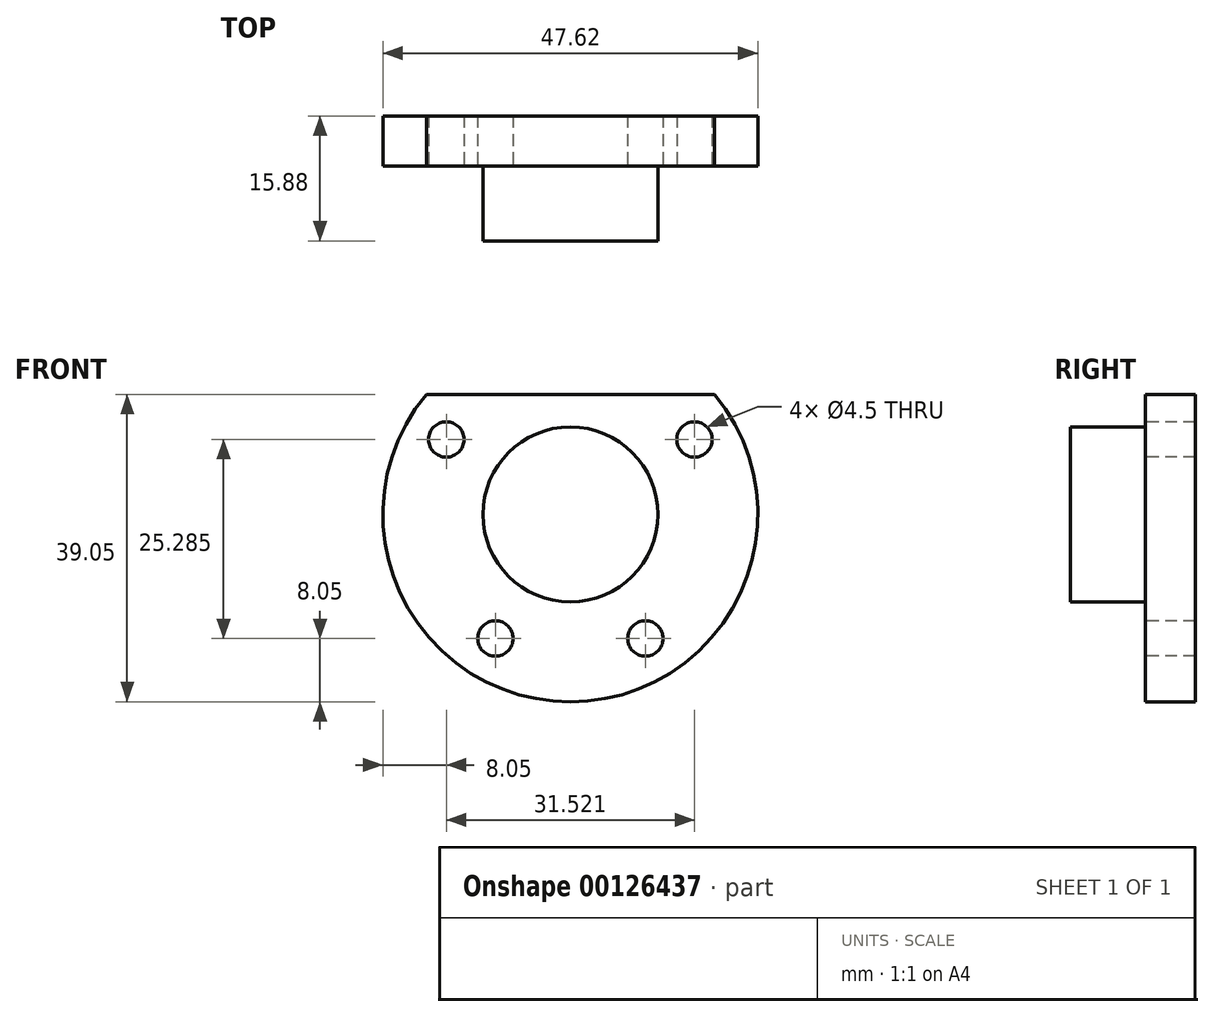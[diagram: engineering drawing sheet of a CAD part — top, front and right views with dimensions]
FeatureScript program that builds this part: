
annotation { "Feature Type Name" : "Feature", "Feature Type Description" : "" }
export const myFeature = defineFeature(function(context is Context, id is Id, definition is map)
    precondition{}
    {
        {
            var Q0;
            Q0=qCreatedBy(makeId("Front.planeOp"),FACE);
            var sketch = newSketch(context, id + "F0", { "sketchPlane" : qUnion([Q0])});
            skArc(sketch, "E0", {"start": v(-18.3, 15.24) * mm, "mid": v(0, -23.81) * mm, "end": v(18.3, 15.24) * mm});
            skLineSegment(sketch, "E1", {"start": v(-18.3, 15.24) * mm, "end": v(18.3, 15.24) * mm});
            skSolve(sketch);
        }
        {
            var Q0;
            Q0 = qSketchRegion(id + "F0", true);
            extrude(context, id + "F1", {"entities" : qUnion([Q0]), "depth" : 6.35 * mm});
        }
        {
            var Q0;
            Q0=makeQuery(id+"F1.opExtrude","CAP_FACE",FACE,{"disambiguationData":[OSD([sQuery(id+"F0.wireOp",EDGE,"E0"),sQuery(id+"F0.wireOp",EDGE,"E1")])],"isStart":false});
            var sketch = newSketch(context, id + "F2", { "sketchPlane" : qUnion([Q0])});
            skCircle(sketch, "E2", {"center": v(0, 0) * mm, "radius": 18.41 * mm, "construction": true});
            skPoint(sketch, "E3", {"position": v(-15.76, 9.52) * mm});
            skPoint(sketch, "E4", {"position": v(-9.52, -15.76) * mm});
            skPoint(sketch, "E5", {"position": v(9.52, -15.76) * mm});
            skPoint(sketch, "E6", {"position": v(15.76, 9.52) * mm});
            skSolve(sketch);
        }
        {
            var Q0;
            Q0=sQuery(id+"F2.wireOp",VERTEX,"E4");
            var Q1;
            Q1=sQuery(id+"F2.wireOp",VERTEX,"E3");
            var Q2;
            Q2=sQuery(id+"F2.wireOp",VERTEX,"E6");
            var Q3;
            Q3=sQuery(id+"F2.wireOp",VERTEX,"E5");
            var Q4;
            Q4=makeQuery(id+"F1.opExtrude","SWEPT_BODY",BODY,{"disambiguationData":[OSD([sQuery(id+"F0.wireOp",EDGE,"E0"),sQuery(id+"F0.wireOp",EDGE,"E1")])]});
            hole(context, id + "F3", {"style" : HoleStyle.SIMPLE, "endStyle" : HoleEndStyle.THROUGH, "standardTappedOrClearance" : lookupTablePath({ "standard" : "ANSI", "fit" : "Normal (ASME)", "size" : "#8", "type" : "Clearance" }), "standardBlindInLast" : lookupTablePath({ "fit" : "Free", "standard" : "ANSI", "size" : "#8", "type" : "Clearance" }), "holeDiameter" : 4.5 * mm, "locations" : qUnion([Q0, Q1, Q2, Q3]), "scope" : qUnion([Q4]), "isTappedThrough" : true});
        }
        {
            var Q0;
            Q0=makeQuery(id+"F1.opExtrude","CAP_FACE",FACE,{"disambiguationData":[OSD([sQuery(id+"F0.wireOp",EDGE,"E0"),sQuery(id+"F0.wireOp",EDGE,"E1")])],"isStart":false});
            var sketch = newSketch(context, id + "F4", { "sketchPlane" : qUnion([Q0])});
            skCircle(sketch, "E7", {"center": v(0, 0) * mm, "radius": 11.11 * mm});
            skSolve(sketch);
        }
        {
            var Q0;
            Q0=makeQuery(id+"F4.imprint","IMPRINT",FACE,{"disambiguationData":[TD([[makeQuery(id+"F4.imprint","IMPRINT",EDGE,{"derivedFrom":sQuery(id+"F4.wireOp",EDGE,"E7")}),1.0]])]});
            extrude(context, id + "F5", {"entities" : qUnion([Q0]), "operationType" : NewBodyOperationType.ADD, "depth" : 9.52 * mm});
        }
    });
